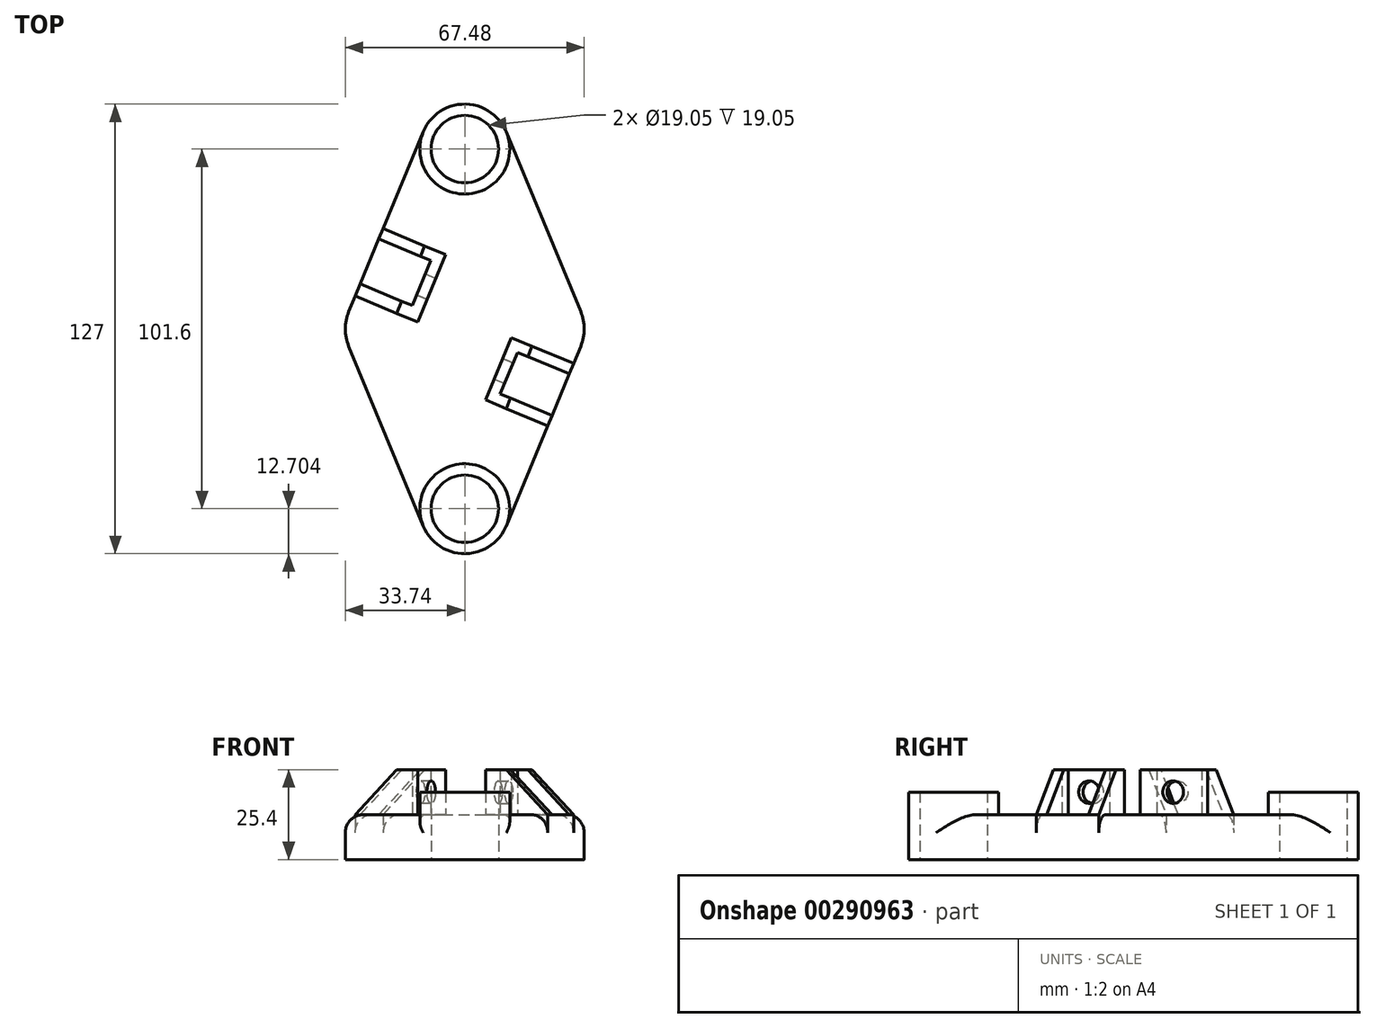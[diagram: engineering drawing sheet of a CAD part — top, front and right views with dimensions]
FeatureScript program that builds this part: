
annotation { "Feature Type Name" : "Feature", "Feature Type Description" : "" }
export const myFeature = defineFeature(function(context is Context, id is Id, definition is map)
    precondition{}
    {
        {
            var Q0;
            Q0=qCreatedBy(makeId("Top.planeOp"),FACE);
            var sketch = newSketch(context, id + "F0", { "sketchPlane" : qUnion([Q0])});
            skCircle(sketch, "E0", {"center": v(0, 63.71) * mm, "radius": 9.53 * mm});
            skCircle(sketch, "E1", {"center": v(0, 63.71) * mm, "radius": 12.7 * mm});
            skCircle(sketch, "E2", {"center": v(0, -37.89) * mm, "radius": 9.53 * mm});
            skCircle(sketch, "E3", {"center": v(0, -37.89) * mm, "radius": 12.7 * mm});
            skLineSegment(sketch, "E4", {"start": v(-11.73, 68.57) * mm, "end": v(-32.78, 17.77) * mm});
            skLineSegment(sketch, "E5", {"start": v(-11.73, -42.75) * mm, "end": v(-32.78, 8.05) * mm});
            skLineSegment(sketch, "E6", {"start": v(11.73, 68.57) * mm, "end": v(32.78, 17.77) * mm});
            skLineSegment(sketch, "E7", {"start": v(32.78, 8.05) * mm, "end": v(11.73, -42.75) * mm});
            skLineSegment(sketch, "E8", {"start": v(-30.94, 22.2) * mm, "end": v(-13.34, 14.9) * mm});
            skLineSegment(sketch, "E9", {"start": v(-13.34, 14.9) * mm, "end": v(-5.45, 33.96) * mm});
            skLineSegment(sketch, "E10", {"start": v(-5.45, 33.96) * mm, "end": v(-23.05, 41.25) * mm});
            skLineSegment(sketch, "E11", {"start": v(30.74, 3.15) * mm, "end": v(13.14, 10.44) * mm});
            skLineSegment(sketch, "E12", {"start": v(13.14, 10.44) * mm, "end": v(5.85, -7.16) * mm});
            skLineSegment(sketch, "E13", {"start": v(0, 63.71) * mm, "end": v(0, -37.89) * mm, "construction": true});
            skLineSegment(sketch, "E14", {"start": v(-29.53, 25.61) * mm, "end": v(-14.86, 19.54) * mm});
            skLineSegment(sketch, "E15", {"start": v(-14.86, 19.54) * mm, "end": v(-9.6, 32.24) * mm});
            skLineSegment(sketch, "E16", {"start": v(-9.6, 32.24) * mm, "end": v(-24.27, 38.31) * mm});
            skLineSegment(sketch, "E17", {"start": v(29.53, 0.21) * mm, "end": v(14.86, 6.29) * mm});
            skLineSegment(sketch, "E18", {"start": v(14.86, 6.29) * mm, "end": v(10, -5.44) * mm});
            skLineSegment(sketch, "E19", {"start": v(10, -5.44) * mm, "end": v(24.67, -11.52) * mm});
            skLineSegment(sketch, "E20", {"start": v(5.85, -7.16) * mm, "end": v(23.45, -14.45) * mm});
            skPoint(sketch, "E21.visualSharp", {"position": v(-34.79, 12.91) * mm});
            skArc(sketch, "E21.filletArc", {"start": v(-32.78, 17.77) * mm, "mid": v(-33.74, 12.91) * mm, "end": v(-32.78, 8.05) * mm});
            skPoint(sketch, "E22.visualSharp", {"position": v(34.79, 12.91) * mm});
            skArc(sketch, "E22.filletArc", {"start": v(32.78, 8.05) * mm, "mid": v(33.74, 12.91) * mm, "end": v(32.78, 17.77) * mm});
            skSolve(sketch);
        }
        {
            var Q0;
            {var subQ2=sQuery(id+"F0.wireOp",EDGE,"E5");Q0=makeQuery(id+"F0.imprint","IMPRINT",FACE,{"disambiguationData":[TD([[makeQuery(id+"F0.imprint","IMPRINT",EDGE,{"derivedFrom":subQ2}),-1.0]])]});}
            extrude(context, id + "F1", {"entities" : qUnion([Q0]), "depth" : 12.7 * mm});
        }
        {
            var Q0;
            Q0=makeQuery(id+"F0.imprint","IMPRINT",FACE,{"disambiguationData":[TD([[makeQuery(id+"F0.imprint","IMPRINT",EDGE,{"derivedFrom":sQuery(id+"F0.wireOp",EDGE,"E0")}),-1.0]])]});
            var Q1;
            Q1=makeQuery(id+"F0.imprint","IMPRINT",FACE,{"disambiguationData":[TD([[makeQuery(id+"F0.imprint","IMPRINT",EDGE,{"derivedFrom":sQuery(id+"F0.wireOp",EDGE,"E2")}),-1.0]])]});
            extrude(context, id + "F2", {"entities" : qUnion([Q0, Q1]), "operationType" : NewBodyOperationType.ADD, "depth" : 19.05 * mm});
        }
        {
            var Q0;
            {var subQ0=sQuery(id+"F0.wireOp",EDGE,"E8");Q0=makeQuery(id+"F0.imprint","IMPRINT",FACE,{"disambiguationData":[TD([[makeQuery(id+"F0.imprint","IMPRINT",EDGE,{"derivedFrom":subQ0}),1.0]])]});}
            var Q1;
            {var subQ0=sQuery(id+"F0.wireOp",EDGE,"E11");Q1=makeQuery(id+"F0.imprint","IMPRINT",FACE,{"disambiguationData":[TD([[makeQuery(id+"F0.imprint","IMPRINT",EDGE,{"derivedFrom":subQ0}),1.0]])]});}
            extrude(context, id + "F3", {"entities" : qUnion([Q0, Q1]), "operationType" : NewBodyOperationType.ADD, "depth" : 25.4 * mm});
        }
        {
            var Q0;
            Q0=makeQuery(id+"F1.opExtrude","CAP_EDGE",EDGE,{"disambiguationData":[OSD([sQuery(id+"F0.wireOp",EDGE,"E6")])],"isStart":false});
            var Q1;
            {var subQ0=sQuery(id+"F0.wireOp",EDGE,"E7");Q1=makeQuery(id+"F1.opExtrude","CAP_EDGE",EDGE,{"disambiguationData":[OSD([subQ0]),TDD([makeQuery(id+"F0.imprint","IMPRINT",EDGE,{"disambiguationData":[TD([[makeQuery(id+"F0.imprint","INTERSECT",VERTEX,{"derivedFrom":[sQuery(id+"F0.wireOp",EDGE,"E3"),subQ0]}),1.0]])],"derivedFrom":subQ0})])],"isStart":false});}
            var Q2;
            Q2=makeQuery(id+"F1.opExtrude","CAP_EDGE",EDGE,{"disambiguationData":[OSD([sQuery(id+"F0.wireOp",EDGE,"E5")])],"isStart":false});
            var Q3;
            Q3=makeQuery(id+"F1.opExtrude","CAP_EDGE",EDGE,{"disambiguationData":[OSD([sQuery(id+"F0.wireOp",EDGE,"E21.filletArc")])],"isStart":false});
            var Q4;
            {var subQ0=sQuery(id+"F0.wireOp",EDGE,"E4");Q4=makeQuery(id+"F1.opExtrude","CAP_EDGE",EDGE,{"disambiguationData":[OSD([subQ0]),TDD([makeQuery(id+"F0.imprint","IMPRINT",EDGE,{"disambiguationData":[TD([[makeQuery(id+"F0.imprint","INTERSECT",VERTEX,{"derivedFrom":[sQuery(id+"F0.wireOp",EDGE,"E1"),subQ0]}),-1.0]])],"derivedFrom":subQ0})])],"isStart":false});}
            fillet(context, id + "F4", {"entities" : qUnion([Q0, Q1, Q2, Q3, Q4]), "radius" : 5.08 * mm, "tangentPropagation" : true, "allowEdgeOverflow" : false});
        }
        {
            var Q0;
            {var subQ0=sQuery(id+"F0.wireOp",EDGE,"E14");Q0=makeQuery(id+"F0.imprint","IMPRINT",FACE,{"disambiguationData":[TD([[makeQuery(id+"F0.imprint","IMPRINT",EDGE,{"derivedFrom":subQ0}),1.0]])]});}
            var Q1;
            {var subQ0=sQuery(id+"F0.wireOp",EDGE,"E17");Q1=makeQuery(id+"F0.imprint","IMPRINT",FACE,{"disambiguationData":[TD([[makeQuery(id+"F0.imprint","IMPRINT",EDGE,{"derivedFrom":subQ0}),1.0]])]});}
            extrude(context, id + "F5", {"entities" : qUnion([Q0, Q1]), "operationType" : NewBodyOperationType.ADD, "depth" : 12.7 * mm});
        }
        {
            var Q0;
            {var subQ0=sQuery(id+"F0.wireOp",EDGE,"E4");Q0=makeQuery(id+"F3.opExtrude","CAP_EDGE",EDGE,{"disambiguationData":[OSD([subQ0]),TDD([makeQuery(id+"F0.imprint","IMPRINT",EDGE,{"disambiguationData":[TD([[makeQuery(id+"F0.imprint","INTERSECT",VERTEX,{"derivedFrom":[subQ0,sQuery(id+"F0.wireOp",EDGE,"E10")]}),-1.0]])],"derivedFrom":subQ0})])],"isStart":false});}
            var Q1;
            {var subQ0=sQuery(id+"F0.wireOp",EDGE,"E4");Q1=makeQuery(id+"F3.opExtrude","CAP_EDGE",EDGE,{"disambiguationData":[OSD([subQ0]),TDD([makeQuery(id+"F0.imprint","IMPRINT",EDGE,{"disambiguationData":[TD([[makeQuery(id+"F0.imprint","INTERSECT",VERTEX,{"derivedFrom":[subQ0,sQuery(id+"F0.wireOp",EDGE,"E8")]}),1.0]])],"derivedFrom":subQ0})])],"isStart":false});}
            var Q2;
            {var subQ0=sQuery(id+"F0.wireOp",EDGE,"E7");Q2=makeQuery(id+"F3.opExtrude","CAP_EDGE",EDGE,{"disambiguationData":[OSD([subQ0]),TDD([makeQuery(id+"F0.imprint","IMPRINT",EDGE,{"disambiguationData":[TD([[makeQuery(id+"F0.imprint","INTERSECT",VERTEX,{"derivedFrom":[subQ0,sQuery(id+"F0.wireOp",EDGE,"E19")]}),-1.0]])],"derivedFrom":subQ0})])],"isStart":false});}
            var Q3;
            {var subQ0=sQuery(id+"F0.wireOp",EDGE,"E7");Q3=makeQuery(id+"F3.opExtrude","CAP_EDGE",EDGE,{"disambiguationData":[OSD([subQ0]),TDD([makeQuery(id+"F0.imprint","IMPRINT",EDGE,{"disambiguationData":[TD([[makeQuery(id+"F0.imprint","INTERSECT",VERTEX,{"derivedFrom":[subQ0,sQuery(id+"F0.wireOp",EDGE,"E11")]}),-1.0]])],"derivedFrom":subQ0})])],"isStart":false});}
            chamfer(context, id + "F6", {"entities" : qUnion([Q0, Q1, Q2, Q3]), "width" : 12.7 * mm, "tangentPropagation" : true});
        }
        {
            var Q0;
            Q0=makeQuery(id+"F3.opExtrude","SWEPT_FACE",FACE,{"disambiguationData":[OSD([sQuery(id+"F0.wireOp",EDGE,"E15")])]});
            var sketch = newSketch(context, id + "F7", { "sketchPlane" : qUnion([Q0])});
            skCircle(sketch, "E23", {"center": v(-18.71, 19.05) * mm, "radius": 3.18 * mm});
            skSolve(sketch);
        }
        {
            var Q0;
            Q0=makeQuery(id+"F7.imprint","IMPRINT",FACE,{"disambiguationData":[TD([[makeQuery(id+"F7.imprint","IMPRINT",EDGE,{"derivedFrom":sQuery(id+"F7.wireOp",EDGE,"E23")}),1.0]])]});
            extrude(context, id + "F8", {"entities" : qUnion([Q0]), "operationType" : NewBodyOperationType.REMOVE, "oppositeDirection" : true, "depth" : 25.4 * mm});
        }
        {
            var Q0;
            Q0=makeQuery(id+"F3.opExtrude","SWEPT_FACE",FACE,{"disambiguationData":[OSD([sQuery(id+"F0.wireOp",EDGE,"E18")])]});
            var sketch = newSketch(context, id + "F9", { "sketchPlane" : qUnion([Q0])});
            skCircle(sketch, "E24", {"center": v(5.15, 19.05) * mm, "radius": 3.17 * mm});
            skSolve(sketch);
        }
        {
            var Q0;
            Q0=makeQuery(id+"F9.imprint","IMPRINT",FACE,{"disambiguationData":[TD([[makeQuery(id+"F9.imprint","IMPRINT",EDGE,{"derivedFrom":sQuery(id+"F9.wireOp",EDGE,"E24")}),1.0]])]});
            extrude(context, id + "F10", {"entities" : qUnion([Q0]), "operationType" : NewBodyOperationType.REMOVE, "oppositeDirection" : true, "depth" : 25.4 * mm});
        }
    });
